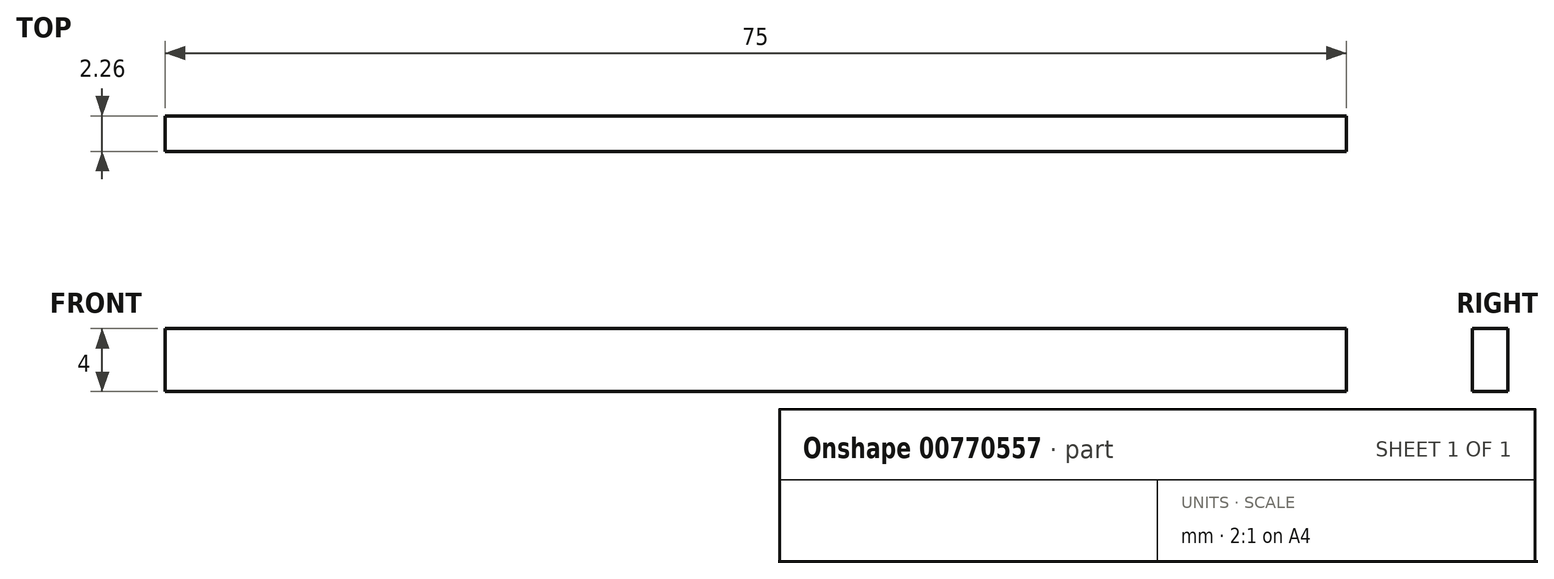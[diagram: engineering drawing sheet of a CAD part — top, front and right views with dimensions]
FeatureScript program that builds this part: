
annotation { "Feature Type Name" : "Feature", "Feature Type Description" : "" }
export const myFeature = defineFeature(function(context is Context, id is Id, definition is map)
    precondition{}
    {
        {
            var Q0;
            Q0=qCreatedBy(makeId("Top.planeOp"),FACE);
            var sketch = newSketch(context, id + "F0", { "sketchPlane" : qUnion([Q0])});
            skLineSegment(sketch, "E0.bottom", {"start": v(0, 0) * mm, "end": v(-75, 0) * mm});
            skLineSegment(sketch, "E0.top", {"start": v(0, 2.26) * mm, "end": v(-75, 2.26) * mm});
            skLineSegment(sketch, "E0.left", {"start": v(0, 0) * mm, "end": v(0, 2.26) * mm});
            skLineSegment(sketch, "E0.right", {"start": v(-75, 0) * mm, "end": v(-75, 2.26) * mm});
            skSolve(sketch);
        }
        {
            var Q0;
            Q0 = qSketchRegion(id + "F0", true);
            extrude(context, id + "F1", {"entities" : qUnion([Q0]), "depth" : 4 * mm, "offsetDistance" : 25 * mm});
        }
    });
